# Revit family: SP2
name_source: partatom
category: Lighting Fixtures
units: mm (PartAtom-declared; Revit-internal decimal feet)

## family parameters
Cut with Voids When Loaded = No
Host = Face
Light Source = Yes
OmniClass Number = 23.80.70.14
OmniClass Title = Luminaries for External Lighting
Part Type = Normal
Room Calculation Point = No
Round Connector Dimension = Use Diameter
Shared = No

## types (1)
- SP2
    Apparent Load = 0 VA
    Color Filter = 16777215
    Default Elevation = 48.00"
    Description = Spectra is designed to enhance contemporary environments during the day while producing comfortable illumination at night. 4 configurable styles of aluminum, natural brushed copper and or stainless steel hoods enable Spectra to carry the lighting designer's vision into a reality. Choice of diffused or indirect sources are capable of producing symmetric or asymmetric distributions. The Spectra family also includes a bollard and large scale luminaire.
    Dimming Lamp Color Temperature Shift = <None>
    Emit Shape Visible in Rendering = No
    Emit from Circle Diameter = 7.00"
    Features = Four hood styles and four lens elements to configure a
look of harmony with your architecture
• Symmetric or asymmetric distribution
• Post-top, wall mount arm, or pole mount arm options
• Adaptable appearance is perfect for contemporary or
traditional installations
• Stainless steel struts
• Powder coat finish in 13 standard colors with a polymer
primer sealer
    Finish = Aluminum-Matte Black
    Glass = Glass-Frosted
    Height = 23.30"
    Hood = Aluminum-Metalic Bronze
    Inner Dia = 16.00"
    Lamp = LED Lamp
    Lens = Glass -  White
    Load Classification = Lighting
    Manufacturer = Architectural Area Lighting
    Model = SP2
    Outter Dia = 23.50"
    Photometric Web File = SP2-ANG-GLA-9LED-BW.IES
    Tilt Angle = 0.00°
    URL = https://www.currentlighting.com
    Voltage = 120 V
    Wattage Comments = 21

## geometry (parser evidence)
native form markers: Blend x30, Sweep x2
no freeform markers — native parametric forms only
